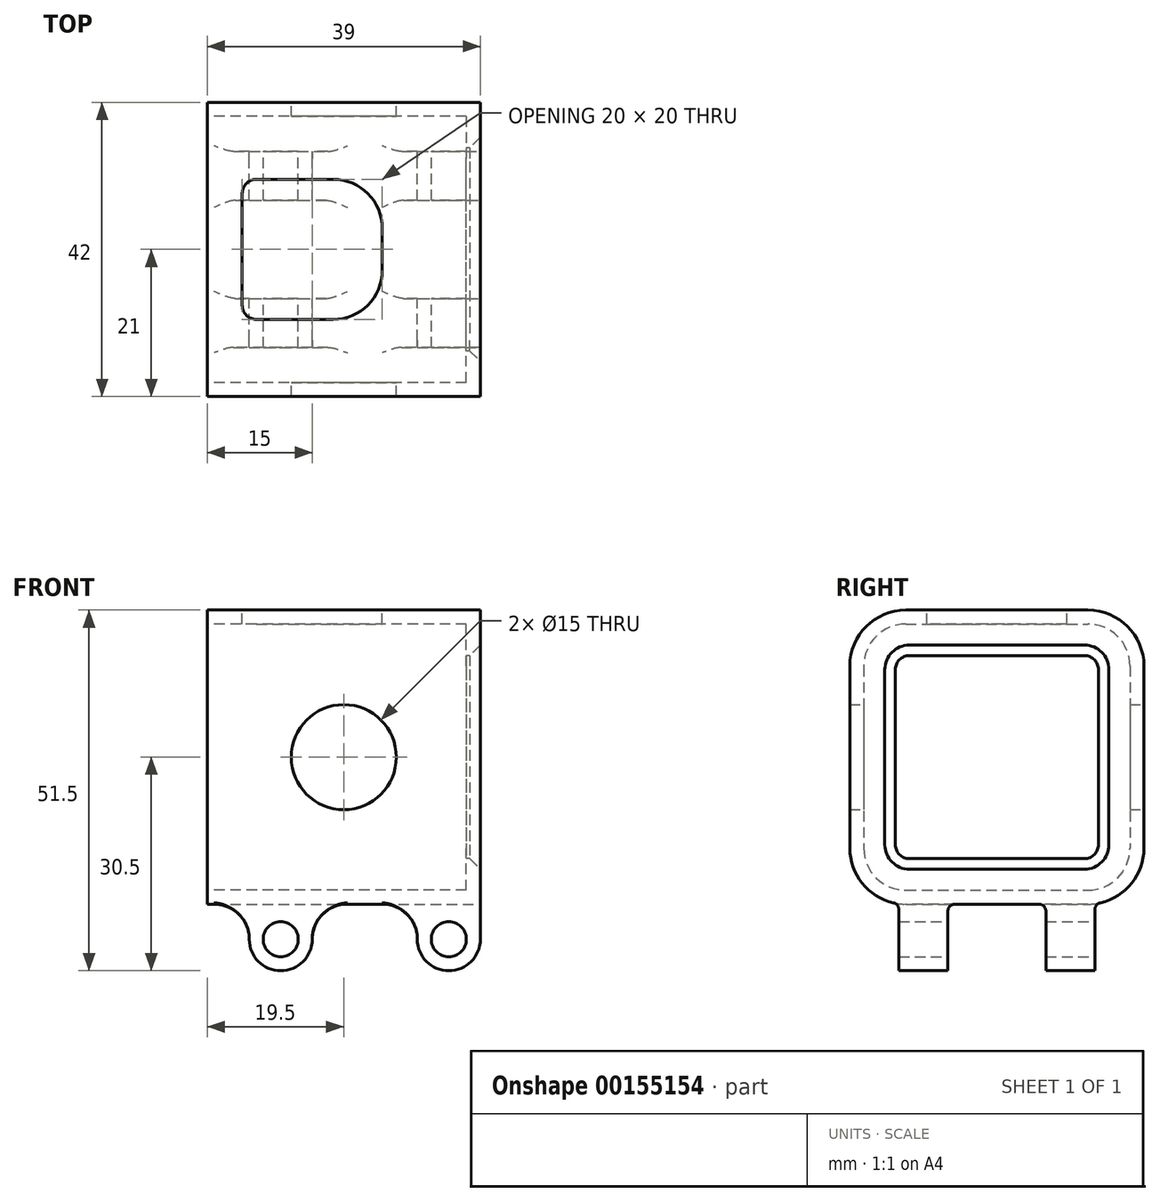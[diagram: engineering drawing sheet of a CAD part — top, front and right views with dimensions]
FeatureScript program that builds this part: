
annotation { "Feature Type Name" : "Feature", "Feature Type Description" : "" }
export const myFeature = defineFeature(function(context is Context, id is Id, definition is map)
    precondition{}
    {
        {
            var Q0;
            Q0=qCreatedBy(makeId("Right.planeOp"),FACE);
            var sketch = newSketch(context, id + "F0", { "sketchPlane" : qUnion([Q0])});
            skLineSegment(sketch, "E0.bottom", {"start": v(-13, 21) * mm, "end": v(13, 21) * mm});
            skLineSegment(sketch, "E0.top", {"start": v(-13, -21) * mm, "end": v(13, -21) * mm});
            skLineSegment(sketch, "E0.left", {"start": v(-21, 13) * mm, "end": v(-21, -13) * mm});
            skLineSegment(sketch, "E0.right", {"start": v(21, 13) * mm, "end": v(21, -13) * mm});
            skLineSegment(sketch, "E1.bottom", {"start": v(-13, 19) * mm, "end": v(13, 19) * mm});
            skLineSegment(sketch, "E1.top", {"start": v(-13, -19) * mm, "end": v(13, -19) * mm});
            skLineSegment(sketch, "E1.left", {"start": v(-19, 13) * mm, "end": v(-19, -13) * mm});
            skLineSegment(sketch, "E1.right", {"start": v(19, 13) * mm, "end": v(19, -13) * mm});
            skPoint(sketch, "E2.visualSharp", {"position": v(-19, 19) * mm});
            skArc(sketch, "E2.filletArc", {"start": v(-13, 19) * mm, "mid": v(-17.24, 17.24) * mm, "end": v(-19, 13) * mm});
            skPoint(sketch, "E3.visualSharp", {"position": v(19, 19) * mm});
            skArc(sketch, "E3.filletArc", {"start": v(19, 13) * mm, "mid": v(17.24, 17.24) * mm, "end": v(13, 19) * mm});
            skPoint(sketch, "E4.visualSharp", {"position": v(19, -19) * mm});
            skArc(sketch, "E4.filletArc", {"start": v(13, -19) * mm, "mid": v(17.24, -17.24) * mm, "end": v(19, -13) * mm});
            skPoint(sketch, "E5.visualSharp", {"position": v(-19, -19) * mm});
            skArc(sketch, "E5.filletArc", {"start": v(-19, -13) * mm, "mid": v(-17.24, -17.24) * mm, "end": v(-13, -19) * mm});
            skPoint(sketch, "E6.visualSharp", {"position": v(-21, -21) * mm});
            skArc(sketch, "E6.filletArc", {"start": v(-21, -13) * mm, "mid": v(-18.66, -18.66) * mm, "end": v(-13, -21) * mm});
            skPoint(sketch, "E7.visualSharp", {"position": v(21, -21) * mm});
            skArc(sketch, "E7.filletArc", {"start": v(13, -21) * mm, "mid": v(18.66, -18.66) * mm, "end": v(21, -13) * mm});
            skPoint(sketch, "E8.visualSharp", {"position": v(21, 21) * mm});
            skArc(sketch, "E8.filletArc", {"start": v(21, 13) * mm, "mid": v(18.66, 18.66) * mm, "end": v(13, 21) * mm});
            skPoint(sketch, "E9.visualSharp", {"position": v(-21, 21) * mm});
            skArc(sketch, "E9.filletArc", {"start": v(-13, 21) * mm, "mid": v(-18.66, 18.66) * mm, "end": v(-21, 13) * mm});
            skSolve(sketch);
        }
        {
            var Q0;
            Q0=qSketchRegion(id+"F0",true);
            extrude(context, id + "F1", {"entities" : qUnion([Q0]), "endBound" : BoundingType.SYMMETRIC, "depth" : 37 * mm});
        }
        {
            var Q0;
            Q0=makeQuery(id+"F1.opExtrude","CAP_FACE",FACE,{"disambiguationData":[OSD([sQuery(id+"F0.wireOp",EDGE,"E0.bottom"),sQuery(id+"F0.wireOp",EDGE,"E0.top"),sQuery(id+"F0.wireOp",EDGE,"E0.left"),sQuery(id+"F0.wireOp",EDGE,"E0.right"),sQuery(id+"F0.wireOp",EDGE,"E1.bottom"),sQuery(id+"F0.wireOp",EDGE,"E1.top"),sQuery(id+"F0.wireOp",EDGE,"E1.left"),sQuery(id+"F0.wireOp",EDGE,"E1.right"),sQuery(id+"F0.wireOp",EDGE,"E2.filletArc"),sQuery(id+"F0.wireOp",EDGE,"E3.filletArc"),sQuery(id+"F0.wireOp",EDGE,"E4.filletArc"),sQuery(id+"F0.wireOp",EDGE,"E5.filletArc"),sQuery(id+"F0.wireOp",EDGE,"E6.filletArc"),sQuery(id+"F0.wireOp",EDGE,"E7.filletArc"),sQuery(id+"F0.wireOp",EDGE,"E8.filletArc"),sQuery(id+"F0.wireOp",EDGE,"E9.filletArc")])],"isStart":false});
            var sketch = newSketch(context, id + "F2", { "sketchPlane" : qUnion([Q0])});
            skLineSegment(sketch, "E10.bottom", {"start": v(-12.5, 14.5) * mm, "end": v(12.5, 14.5) * mm});
            skLineSegment(sketch, "E10.top", {"start": v(-12.5, -14.5) * mm, "end": v(12.5, -14.5) * mm});
            skLineSegment(sketch, "E10.left", {"start": v(-14.5, 12.5) * mm, "end": v(-14.5, -12.5) * mm});
            skLineSegment(sketch, "E10.right", {"start": v(14.5, 12.5) * mm, "end": v(14.5, -12.5) * mm});
            skLineSegment(sketch, "E11.bottom", {"start": v(-13, 21) * mm, "end": v(13, 21) * mm});
            skLineSegment(sketch, "E11.top", {"start": v(-13, -21) * mm, "end": v(13, -21) * mm});
            skLineSegment(sketch, "E11.left", {"start": v(-21, 13) * mm, "end": v(-21, -13) * mm});
            skLineSegment(sketch, "E11.right", {"start": v(21, 13) * mm, "end": v(21, -13) * mm});
            skPoint(sketch, "E12.visualSharp", {"position": v(-21, 21) * mm});
            skArc(sketch, "E12.filletArc", {"start": v(-13, 21) * mm, "mid": v(-18.66, 18.66) * mm, "end": v(-21, 13) * mm});
            skPoint(sketch, "E13.visualSharp", {"position": v(-21, -21) * mm});
            skArc(sketch, "E13.filletArc", {"start": v(-21, -13) * mm, "mid": v(-18.66, -18.66) * mm, "end": v(-13, -21) * mm});
            skPoint(sketch, "E14.visualSharp", {"position": v(21, -21) * mm});
            skArc(sketch, "E14.filletArc", {"start": v(13, -21) * mm, "mid": v(18.66, -18.66) * mm, "end": v(21, -13) * mm});
            skPoint(sketch, "E15.visualSharp", {"position": v(21, 21) * mm});
            skArc(sketch, "E15.filletArc", {"start": v(21, 13) * mm, "mid": v(18.66, 18.66) * mm, "end": v(13, 21) * mm});
            skPoint(sketch, "E16.visualSharp", {"position": v(-14.5, 14.5) * mm});
            skArc(sketch, "E16.filletArc", {"start": v(-12.5, 14.5) * mm, "mid": v(-13.91, 13.91) * mm, "end": v(-14.5, 12.5) * mm});
            skPoint(sketch, "E17.visualSharp", {"position": v(-14.5, -14.5) * mm});
            skArc(sketch, "E17.filletArc", {"start": v(-14.5, -12.5) * mm, "mid": v(-13.91, -13.91) * mm, "end": v(-12.5, -14.5) * mm});
            skPoint(sketch, "E18.visualSharp", {"position": v(14.5, -14.5) * mm});
            skArc(sketch, "E18.filletArc", {"start": v(12.5, -14.5) * mm, "mid": v(13.91, -13.91) * mm, "end": v(14.5, -12.5) * mm});
            skPoint(sketch, "E19.visualSharp", {"position": v(14.5, 14.5) * mm});
            skArc(sketch, "E19.filletArc", {"start": v(14.5, 12.5) * mm, "mid": v(13.91, 13.91) * mm, "end": v(12.5, 14.5) * mm});
            skSolve(sketch);
        }
        {
            var Q0;
            Q0=qSketchRegion(id+"F2",true);
            extrude(context, id + "F3", {"entities" : qUnion([Q0]), "operationType" : NewBodyOperationType.ADD, "depth" : 2 * mm});
        }
        {
            var Q0;
            Q0=makeQuery(id+"F3.opExtrude","CAP_EDGE",EDGE,{"disambiguationData":[OSD([sQuery(id+"F2.wireOp",EDGE,"E10.bottom")])],"isStart":false});
            chamfer(context, id + "F4", {"entities" : qUnion([Q0]), "width" : 1.5 * mm, "tangentPropagation" : true});
        }
        {
            var Q0;
            Q0=makeQuery(id+"F3.boolean.opBoolean","MERGE",FACE,{"derivedFrom":[makeQuery(id+"F1.opExtrude","SWEPT_FACE",FACE,{"disambiguationData":[OSD([sQuery(id+"F0.wireOp",EDGE,"E0.bottom")])]}),makeQuery(id+"F3.opExtrude","SWEPT_FACE",FACE,{"disambiguationData":[OSD([sQuery(id+"F2.wireOp",EDGE,"E11.bottom")])]})]});
            var sketch = newSketch(context, id + "F5", { "sketchPlane" : qUnion([Q0])});
            skLineSegment(sketch, "E20.bottom", {"start": v(-11.5, 10) * mm, "end": v(-0.5, 10) * mm});
            skLineSegment(sketch, "E20.top", {"start": v(-11.5, -10) * mm, "end": v(-0.5, -10) * mm});
            skLineSegment(sketch, "E20.left", {"start": v(-13.5, 8) * mm, "end": v(-13.5, -8) * mm});
            skLineSegment(sketch, "E20.right", {"start": v(6.5, 3) * mm, "end": v(6.5, -3) * mm});
            skPoint(sketch, "E21.visualSharp", {"position": v(-13.5, 10) * mm});
            skArc(sketch, "E21.filletArc", {"start": v(-11.5, 10) * mm, "mid": v(-12.91, 9.41) * mm, "end": v(-13.5, 8) * mm});
            skPoint(sketch, "E22.visualSharp", {"position": v(-13.5, -10) * mm});
            skArc(sketch, "E22.filletArc", {"start": v(-13.5, -8) * mm, "mid": v(-12.91, -9.41) * mm, "end": v(-11.5, -10) * mm});
            skPoint(sketch, "E23.visualSharp", {"position": v(6.5, 10) * mm});
            skArc(sketch, "E23.filletArc", {"start": v(6.5, 3) * mm, "mid": v(4.45, 7.95) * mm, "end": v(-0.5, 10) * mm});
            skPoint(sketch, "E24.visualSharp", {"position": v(6.5, -10) * mm});
            skArc(sketch, "E24.filletArc", {"start": v(-0.5, -10) * mm, "mid": v(4.45, -7.95) * mm, "end": v(6.5, -3) * mm});
            skSolve(sketch);
        }
        {
            var Q0;
            Q0=qSketchRegion(id+"F5",true);
            extrude(context, id + "F6", {"entities" : qUnion([Q0]), "operationType" : NewBodyOperationType.REMOVE, "oppositeDirection" : true, "depth" : 5 * mm});
        }
        {
            var Q0;
            Q0=qCreatedBy(makeId("Front.planeOp"),FACE);
            var sketch = newSketch(context, id + "F7", { "sketchPlane" : qUnion([Q0])});
            skCircle(sketch, "E25", {"center": v(16, -26) * mm, "radius": 2.5 * mm});
            skCircle(sketch, "E26", {"center": v(-8, -26) * mm, "radius": 2.5 * mm});
            skLineSegment(sketch, "E27", {"start": v(-8, -26) * mm, "end": v(16, -26) * mm, "construction": true});
            skArc(sketch, "E28", {"start": v(11.5, -26) * mm, "mid": v(16, -30.5) * mm, "end": v(20.5, -26) * mm});
            skArc(sketch, "E29", {"start": v(-12.5, -26) * mm, "mid": v(-8, -30.5) * mm, "end": v(-3.5, -26) * mm});
            skLineSegment(sketch, "E30", {"start": v(20.5, -26) * mm, "end": v(20.5, -20) * mm});
            skLineSegment(sketch, "E31", {"start": v(11.5, -26) * mm, "end": v(11.5, -20) * mm});
            skLineSegment(sketch, "E32", {"start": v(-3.5, -26) * mm, "end": v(-3.5, -20) * mm});
            skLineSegment(sketch, "E33", {"start": v(-3.5, -20) * mm, "end": v(-12.5, -20) * mm});
            skLineSegment(sketch, "E34", {"start": v(-12.5, -20) * mm, "end": v(-12.5, -26) * mm});
            skLineSegment(sketch, "E35", {"start": v(-3.5, -20) * mm, "end": v(11.5, -20) * mm, "construction": true});
            skLineSegment(sketch, "E36", {"start": v(11.5, -20) * mm, "end": v(20.5, -20) * mm});
            skPoint(sketch, "E36.endSnap0", {"position": v(4, -20) * mm});
            skSolve(sketch);
        }
        {
            var Q0;
            Q0=qSketchRegion(id+"F7",true);
            extrude(context, id + "F8", {"entities" : qUnion([Q0]), "operationType" : NewBodyOperationType.ADD, "endBound" : BoundingType.SYMMETRIC, "depth" : 28 * mm});
        }
        {
            var Q0;
            Q0=makeQuery(id+"F8.boolean.opBoolean","INTERSECT",EDGE,{"derivedFrom":[makeQuery(id+"F3.boolean.opBoolean","MERGE",FACE,{"derivedFrom":[makeQuery(id+"F1.opExtrude","SWEPT_FACE",FACE,{"disambiguationData":[OSD([sQuery(id+"F0.wireOp",EDGE,"E0.top")])]}),makeQuery(id+"F3.opExtrude","SWEPT_FACE",FACE,{"disambiguationData":[OSD([sQuery(id+"F2.wireOp",EDGE,"E11.top")])]})]}),makeQuery(id+"F8.opExtrude","SWEPT_FACE",FACE,{"disambiguationData":[OSD([sQuery(id+"F7.wireOp",EDGE,"E34")])]})]});
            var Q1;
            Q1=makeQuery(id+"F8.boolean.opBoolean","INTERSECT",EDGE,{"derivedFrom":[makeQuery(id+"F3.boolean.opBoolean","MERGE",FACE,{"derivedFrom":[makeQuery(id+"F1.opExtrude","SWEPT_FACE",FACE,{"disambiguationData":[OSD([sQuery(id+"F0.wireOp",EDGE,"E0.top")])]}),makeQuery(id+"F3.opExtrude","SWEPT_FACE",FACE,{"disambiguationData":[OSD([sQuery(id+"F2.wireOp",EDGE,"E11.top")])]})]}),makeQuery(id+"F8.opExtrude","SWEPT_FACE",FACE,{"disambiguationData":[OSD([sQuery(id+"F7.wireOp",EDGE,"E32")])]})]});
            var Q2;
            Q2=makeQuery(id+"F8.boolean.opBoolean","INTERSECT",EDGE,{"derivedFrom":[makeQuery(id+"F3.boolean.opBoolean","MERGE",FACE,{"derivedFrom":[makeQuery(id+"F1.opExtrude","SWEPT_FACE",FACE,{"disambiguationData":[OSD([sQuery(id+"F0.wireOp",EDGE,"E0.top")])]}),makeQuery(id+"F3.opExtrude","SWEPT_FACE",FACE,{"disambiguationData":[OSD([sQuery(id+"F2.wireOp",EDGE,"E11.top")])]})]}),makeQuery(id+"F8.opExtrude","SWEPT_FACE",FACE,{"disambiguationData":[OSD([sQuery(id+"F7.wireOp",EDGE,"E31")])]})]});
            fillet(context, id + "F9", {"entities" : qUnion([Q0, Q1, Q2]), "radius" : 5 * mm, "tangentPropagation" : true, "allowEdgeOverflow" : false});
        }
        {
            var Q0;
            Q0=makeQuery(id+"F8.boolean.opBoolean","SPLIT",FACE,{"disambiguationData":[TD([makeQuery(id+"F8.opExtrude","SWEPT_FACE",FACE,{"disambiguationData":[OSD([sQuery(id+"F7.wireOp",EDGE,"E31")])]})])],"derivedFrom":makeQuery(id+"F3.boolean.opBoolean","MERGE",FACE,{"derivedFrom":[makeQuery(id+"F1.opExtrude","SWEPT_FACE",FACE,{"disambiguationData":[OSD([sQuery(id+"F0.wireOp",EDGE,"E0.top")])]}),makeQuery(id+"F3.opExtrude","SWEPT_FACE",FACE,{"disambiguationData":[OSD([sQuery(id+"F2.wireOp",EDGE,"E11.top")])]})]})});
            var sketch = newSketch(context, id + "F10", { "sketchPlane" : qUnion([Q0])});
            skLineSegment(sketch, "E37.bottom", {"start": v(-18.5, 7) * mm, "end": v(20.5, 7) * mm});
            skLineSegment(sketch, "E37.top", {"start": v(-18.5, -7) * mm, "end": v(20.5, -7) * mm});
            skLineSegment(sketch, "E37.left", {"start": v(-18.5, 7) * mm, "end": v(-18.5, -7) * mm});
            skLineSegment(sketch, "E37.right", {"start": v(20.5, 7) * mm, "end": v(20.5, -7) * mm});
            skSolve(sketch);
        }
        {
            var Q0;
            Q0 = qSketchRegion(id + "F10", true);
            extrude(context, id + "F11", {"entities" : qUnion([Q0]), "operationType" : NewBodyOperationType.REMOVE, "depth" : 25 * mm});
        }
        {
            var Q0;
            {var subQ2=sQuery(id+"F10.wireOp",EDGE,"E37.bottom");Q0=makeQuery(id+"F11.boolean.opBoolean","COPY",EDGE,{"disambiguationData":[TD([makeQuery(id+"F8.opExtrude","SWEPT_FACE",FACE,{"disambiguationData":[OSD([sQuery(id+"F7.wireOp",EDGE,"E30")])]})])],"derivedFrom":makeQuery(id+"F11.opExtrude","CAP_EDGE",EDGE,{"disambiguationData":[OSD([subQ2])],"isStart":true})});}
            var Q1;
            {var subQ2=sQuery(id+"F10.wireOp",EDGE,"E37.top");Q1=makeQuery(id+"F11.boolean.opBoolean","COPY",EDGE,{"disambiguationData":[TD([makeQuery(id+"F8.opExtrude","SWEPT_FACE",FACE,{"disambiguationData":[OSD([sQuery(id+"F7.wireOp",EDGE,"E30")])]})])],"derivedFrom":makeQuery(id+"F11.opExtrude","CAP_EDGE",EDGE,{"disambiguationData":[OSD([subQ2])],"isStart":true})});}
            var Q2;
            {var subQ0=sQuery(id+"F2.wireOp",EDGE,"E11.top");var subQ1=sQuery(id+"F0.wireOp",EDGE,"E0.top");var subQ2=sQuery(id+"F10.wireOp",EDGE,"E37.bottom");Q2=makeQuery(id+"F11.boolean.opBoolean","COPY",EDGE,{"disambiguationData":[TD([makeQuery(id+"F9.opFillet","BLEND_FACE",FACE,{"disambiguationData":[OSD([subQ1,subQ0,sQuery(id+"F7.wireOp",EDGE,"E32")])]})])],"derivedFrom":makeQuery(id+"F11.opExtrude","CAP_EDGE",EDGE,{"disambiguationData":[OSD([subQ2])],"isStart":true})});}
            var Q3;
            {var subQ0=sQuery(id+"F2.wireOp",EDGE,"E11.top");var subQ1=sQuery(id+"F0.wireOp",EDGE,"E0.top");var subQ2=sQuery(id+"F10.wireOp",EDGE,"E37.top");Q3=makeQuery(id+"F11.boolean.opBoolean","COPY",EDGE,{"disambiguationData":[TD([makeQuery(id+"F9.opFillet","BLEND_FACE",FACE,{"disambiguationData":[OSD([subQ1,subQ0,sQuery(id+"F7.wireOp",EDGE,"E32")])]})])],"derivedFrom":makeQuery(id+"F11.opExtrude","CAP_EDGE",EDGE,{"disambiguationData":[OSD([subQ2])],"isStart":true})});}
            var Q4;
            Q4=makeQuery(id+"F8.boolean.opBoolean","INTERSECT",EDGE,{"derivedFrom":[makeQuery(id+"F3.boolean.opBoolean","MERGE",FACE,{"derivedFrom":[makeQuery(id+"F1.opExtrude","SWEPT_FACE",FACE,{"disambiguationData":[OSD([sQuery(id+"F0.wireOp",EDGE,"E6.filletArc")])]}),makeQuery(id+"F3.opExtrude","SWEPT_FACE",FACE,{"disambiguationData":[OSD([sQuery(id+"F2.wireOp",EDGE,"E13.filletArc")])]})]}),makeQuery(id+"F8.opExtrude","CAP_FACE",FACE,{"disambiguationData":[OSD([sQuery(id+"F7.wireOp",EDGE,"E25"),sQuery(id+"F7.wireOp",EDGE,"E28"),sQuery(id+"F7.wireOp",EDGE,"E30"),sQuery(id+"F7.wireOp",EDGE,"E31"),sQuery(id+"F7.wireOp",EDGE,"E36")])],"isStart":false})]});
            var Q5;
            Q5=makeQuery(id+"F8.boolean.opBoolean","INTERSECT",EDGE,{"derivedFrom":[makeQuery(id+"F3.boolean.opBoolean","MERGE",FACE,{"derivedFrom":[makeQuery(id+"F1.opExtrude","SWEPT_FACE",FACE,{"disambiguationData":[OSD([sQuery(id+"F0.wireOp",EDGE,"E6.filletArc")])]}),makeQuery(id+"F3.opExtrude","SWEPT_FACE",FACE,{"disambiguationData":[OSD([sQuery(id+"F2.wireOp",EDGE,"E13.filletArc")])]})]}),makeQuery(id+"F8.opExtrude","CAP_FACE",FACE,{"disambiguationData":[OSD([sQuery(id+"F7.wireOp",EDGE,"E26"),sQuery(id+"F7.wireOp",EDGE,"E29"),sQuery(id+"F7.wireOp",EDGE,"E32"),sQuery(id+"F7.wireOp",EDGE,"E33"),sQuery(id+"F7.wireOp",EDGE,"E34")])],"isStart":false})]});
            var Q6;
            Q6=makeQuery(id+"F8.boolean.opBoolean","INTERSECT",EDGE,{"derivedFrom":[makeQuery(id+"F3.boolean.opBoolean","MERGE",FACE,{"derivedFrom":[makeQuery(id+"F1.opExtrude","SWEPT_FACE",FACE,{"disambiguationData":[OSD([sQuery(id+"F0.wireOp",EDGE,"E7.filletArc")])]}),makeQuery(id+"F3.opExtrude","SWEPT_FACE",FACE,{"disambiguationData":[OSD([sQuery(id+"F2.wireOp",EDGE,"E14.filletArc")])]})]}),makeQuery(id+"F8.opExtrude","CAP_FACE",FACE,{"disambiguationData":[OSD([sQuery(id+"F7.wireOp",EDGE,"E26"),sQuery(id+"F7.wireOp",EDGE,"E29"),sQuery(id+"F7.wireOp",EDGE,"E32"),sQuery(id+"F7.wireOp",EDGE,"E33"),sQuery(id+"F7.wireOp",EDGE,"E34")])],"isStart":true})]});
            var Q7;
            Q7=makeQuery(id+"F8.boolean.opBoolean","INTERSECT",EDGE,{"derivedFrom":[makeQuery(id+"F3.boolean.opBoolean","MERGE",FACE,{"derivedFrom":[makeQuery(id+"F1.opExtrude","SWEPT_FACE",FACE,{"disambiguationData":[OSD([sQuery(id+"F0.wireOp",EDGE,"E7.filletArc")])]}),makeQuery(id+"F3.opExtrude","SWEPT_FACE",FACE,{"disambiguationData":[OSD([sQuery(id+"F2.wireOp",EDGE,"E14.filletArc")])]})]}),makeQuery(id+"F8.opExtrude","CAP_FACE",FACE,{"disambiguationData":[OSD([sQuery(id+"F7.wireOp",EDGE,"E25"),sQuery(id+"F7.wireOp",EDGE,"E28"),sQuery(id+"F7.wireOp",EDGE,"E30"),sQuery(id+"F7.wireOp",EDGE,"E31"),sQuery(id+"F7.wireOp",EDGE,"E36")])],"isStart":true})]});
            fillet(context, id + "F12", {"entities" : qUnion([Q0, Q1, Q2, Q3, Q4, Q5, Q6, Q7]), "radius" : 1 * mm, "tangentPropagation" : true, "allowEdgeOverflow" : false});
        }
        {
            var Q0;
            Q0=qCreatedBy(makeId("Front.planeOp"),FACE);
            var sketch = newSketch(context, id + "F13", { "sketchPlane" : qUnion([Q0])});
            skCircle(sketch, "E38", {"center": v(1, 0) * mm, "radius": 7.5 * mm});
            skSolve(sketch);
        }
        {
            var Q0;
            Q0 = qSketchRegion(id + "F13", true);
            extrude(context, id + "F14", {"entities" : qUnion([Q0]), "operationType" : NewBodyOperationType.REMOVE, "endBound" : BoundingType.SYMMETRIC, "depth" : 45 * mm});
        }
    });
